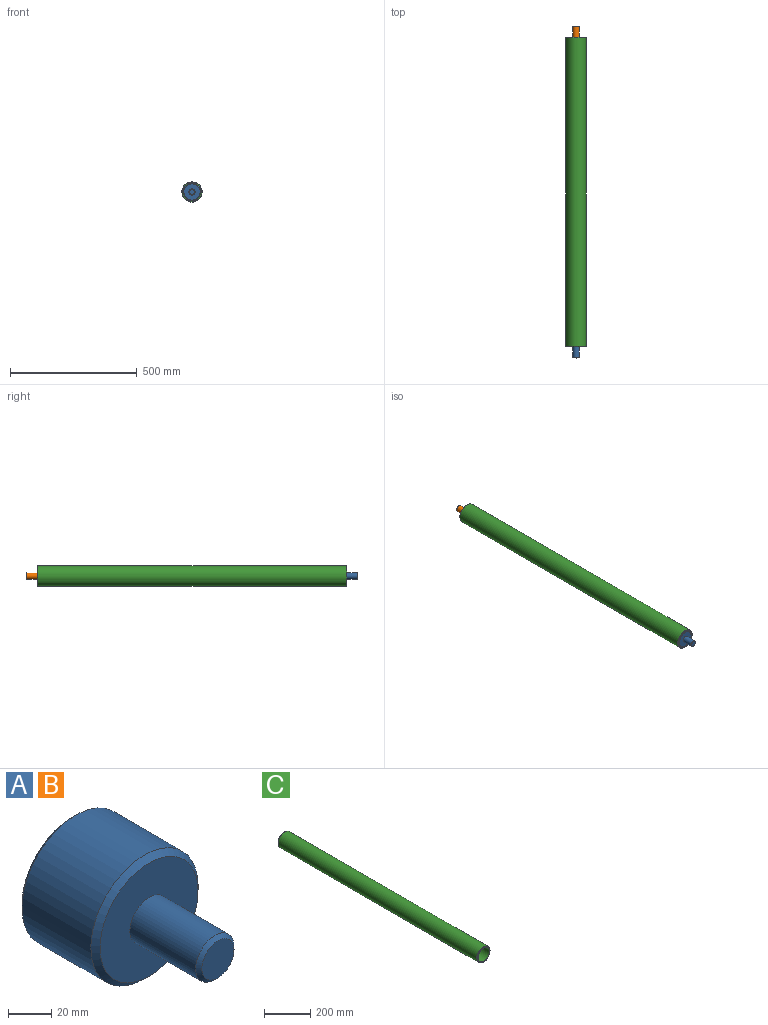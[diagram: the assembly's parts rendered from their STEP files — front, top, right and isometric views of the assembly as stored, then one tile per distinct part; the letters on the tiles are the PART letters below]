
ASSEMBLY  parts=3 mates=1
PART A: 10 faces, bbox 70x95x70 mm
  f0: cylinder r=35mm len=70mm, axis (0,1,0), area 9896mm2, adj f7,f9
  f1: plane 64x64mm, normal (0,-1,0), area 2726.1mm2, adj f5,f7
  f2: plane 66x66mm, normal (0,1,0), area 779.1mm2, adj f3,f9
  f3: cylinder r=29mm len=58mm, axis (0,1,0), area 7652.9mm2, adj f2,f4
  f4: plane 58x58mm, normal (0,1,0), area 2642.1mm2, adj f3
  f5: cylinder r=12.5mm len=43mm, axis (0,1,0), area 3377.2mm2, adj f1,f8
  f6: plane 21x21mm, normal (0,-1,0), area 346.4mm2, adj f8
  f7: cone r=32mm half-angle=45deg, axis (0,1,0), area 893mm2, adj f0,f1
  f8: cone r=10.5mm half-angle=45deg, axis (0,1,0), area 204.4mm2, adj f5,f6
  f9: cone r=35mm half-angle=45deg, axis (0,-1,0), area 604.2mm2, adj f0,f2
PART B: same geometry as A
PART C: 6 faces, bbox 80x1220x80 mm
  f0: cylinder r=35mm len=1220mm, axis (0,1,0), area 268292mm2, adj f2,f3
  f1: cylinder r=40mm len=1216mm, axis (0,1,0), area 305614.1mm2, adj f4,f5
  f2: plane 76x76mm, normal (0,-1,0), area 688mm2, adj f0,f4
  f3: plane 76x76mm, normal (0,1,0), area 688mm2, adj f0,f5
  f4: cone r=38mm half-angle=45deg, axis (0,1,0), area 693.1mm2, adj f1,f2
  f5: cone r=40mm half-angle=45deg, axis (0,-1,0), area 693.1mm2, adj f1,f3
PLACE A t=(-676.75,-376.56,-163.26)mm
PLACE B rot(axis=(0,0,1),180deg) t=(-676.75,743.44,-163.26)mm
PLACE C t=(-676.75,793.44,-163.26)mm
MATE cylindrical C.f1 <-> A.f0  axis (0,-1,0) through (-676.75,-426.56,-163.26)mm
